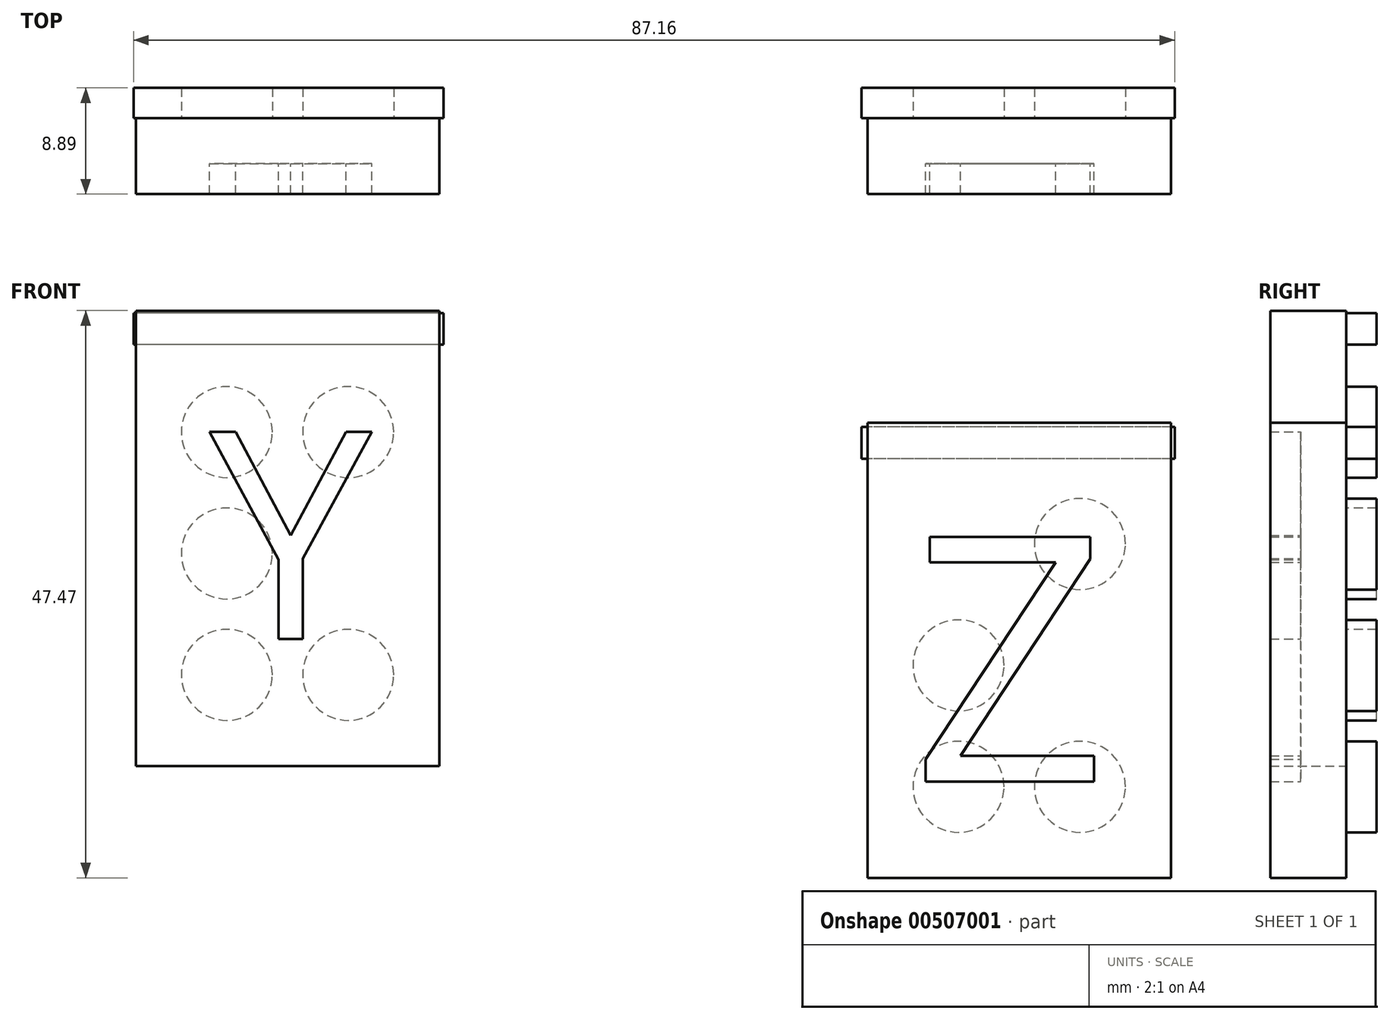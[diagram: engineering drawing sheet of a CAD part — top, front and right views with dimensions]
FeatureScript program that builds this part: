
annotation { "Feature Type Name" : "Feature", "Feature Type Description" : "" }
export const myFeature = defineFeature(function(context is Context, id is Id, definition is map)
    precondition{}
    {
        {
            var Q0;
            Q0=qCreatedBy(makeId("Front.planeOp"),FACE);
            var sketch = newSketch(context, id + "F0", { "sketchPlane" : qUnion([Q0])});
            skLineSegment(sketch, "E0.bottom", {"start": v(-41.67, 25.1) * mm, "end": v(-16.27, 25.1) * mm});
            skLineSegment(sketch, "E0.top", {"start": v(-41.67, -13) * mm, "end": v(-16.27, -13) * mm});
            skLineSegment(sketch, "E0.left", {"start": v(-41.67, 25.1) * mm, "end": v(-41.67, -13) * mm});
            skLineSegment(sketch, "E0.right", {"start": v(-16.27, 25.1) * mm, "end": v(-16.27, -13) * mm});
            skLineSegment(sketch, "E1.bottom", {"start": v(19.58, 15.74) * mm, "end": v(44.98, 15.74) * mm});
            skLineSegment(sketch, "E1.top", {"start": v(19.58, -22.36) * mm, "end": v(44.98, -22.36) * mm});
            skLineSegment(sketch, "E1.left", {"start": v(19.58, 15.74) * mm, "end": v(19.58, -22.36) * mm});
            skLineSegment(sketch, "E1.right", {"start": v(44.98, 15.74) * mm, "end": v(44.98, -22.36) * mm});
            skSolve(sketch);
        }
        {
            var Q0;
            Q0 = qSketchRegion(id + "F0", true);
            extrude(context, id + "F1", {"entities" : qUnion([Q0]), "depth" : 6.35 * mm});
        }
        {
            var Q0;
            Q0=qCreatedBy(makeId("Front.planeOp"),FACE);
            var sketch = newSketch(context, id + "F2", { "sketchPlane" : qUnion([Q0])});
            skCircle(sketch, "E2", {"center": v(-34.05, 14.95) * mm, "radius": 3.81 * mm});
            skCircle(sketch, "E3", {"center": v(37.36, 5.58) * mm, "radius": 3.81 * mm});
            skCircle(sketch, "E4", {"center": v(27.2, -4.58) * mm, "radius": 3.81 * mm});
            skCircle(sketch, "E5", {"center": v(37.36, -14.74) * mm, "radius": 3.81 * mm});
            skCircle(sketch, "E6", {"center": v(27.2, -14.74) * mm, "radius": 3.8 * mm});
            skCircle(sketch, "E7", {"center": v(-34.05, -5.37) * mm, "radius": 3.8 * mm});
            skCircle(sketch, "E8", {"center": v(-23.89, -5.37) * mm, "radius": 3.81 * mm});
            skCircle(sketch, "E9", {"center": v(-34.05, 4.79) * mm, "radius": 3.81 * mm});
            skCircle(sketch, "E10", {"center": v(-23.89, 14.95) * mm, "radius": 3.81 * mm});
            skSolve(sketch);
        }
        {
            var Q0;
            Q0 = qSketchRegion(id + "F2", true);
            extrude(context, id + "F3", {"entities" : qUnion([Q0]), "operationType" : NewBodyOperationType.ADD, "oppositeDirection" : true, "depth" : 2.54 * mm});
        }
        {
            var Q0;
            Q0=qCreatedBy(makeId("Front.planeOp"),FACE);
            cPlane(context, id + "F4", {"entities" : qUnion([Q0]), "cplaneType" : CPlaneType.OFFSET, "offset" : 3.8 * mm, "width" : 152.4 * mm, "height" : 152.4 * mm});
        }
        {
            var Q0;
            Q0=qCreatedBy(id+"F4.planeOp",FACE);
            var sketch = newSketch(context, id + "F5", { "sketchPlane" : qUnion([Q0])});
            skText(sketch, "E11", { "text": "Y", "fontName": "OpenSans-Regular.ttf"});
            skText(sketch, "E12", { "text": "Z", "fontName": "OpenSans-Regular.ttf"});
            const initialGuessF5  = {"E11": [-0.0355, -0.00238, 1, 0, 0.01749], "E12": [0.02331, -0.0143, 1, 0, 0.02066]};
            skSetInitialGuess(sketch, initialGuessF5);
            skSolve(sketch);
        }
        {
            var Q0;
            Q0 = qSketchRegion(id + "F5", true);
            extrude(context, id + "F6", {"entities" : qUnion([Q0]), "operationType" : NewBodyOperationType.REMOVE, "depth" : 25.4 * mm});
        }
        {
            var Q0;
            Q0=qCreatedBy(makeId("Front.planeOp"),FACE);
            var sketch = newSketch(context, id + "F7", { "sketchPlane" : qUnion([Q0])});
            skLineSegment(sketch, "E13.bottom", {"start": v(45.3, 15.37) * mm, "end": v(19.08, 15.37) * mm});
            skLineSegment(sketch, "E13.top", {"start": v(45.3, 12.72) * mm, "end": v(19.08, 12.72) * mm});
            skLineSegment(sketch, "E13.left", {"start": v(45.3, 15.37) * mm, "end": v(45.3, 12.72) * mm});
            skLineSegment(sketch, "E13.right", {"start": v(19.08, 15.37) * mm, "end": v(19.08, 12.72) * mm});
            skLineSegment(sketch, "E14.bottom", {"start": v(-15.9, 24.9) * mm, "end": v(-41.86, 24.9) * mm});
            skLineSegment(sketch, "E14.top", {"start": v(-15.9, 22.25) * mm, "end": v(-41.86, 22.25) * mm});
            skLineSegment(sketch, "E14.left", {"start": v(-15.9, 24.9) * mm, "end": v(-15.9, 22.25) * mm});
            skLineSegment(sketch, "E14.right", {"start": v(-41.86, 24.9) * mm, "end": v(-41.86, 22.25) * mm});
            skSolve(sketch);
        }
        {
            var Q0;
            Q0 = qSketchRegion(id + "F7", true);
            extrude(context, id + "F8", {"entities" : qUnion([Q0]), "operationType" : NewBodyOperationType.ADD, "oppositeDirection" : true, "depth" : 2.54 * mm});
        }
    });
